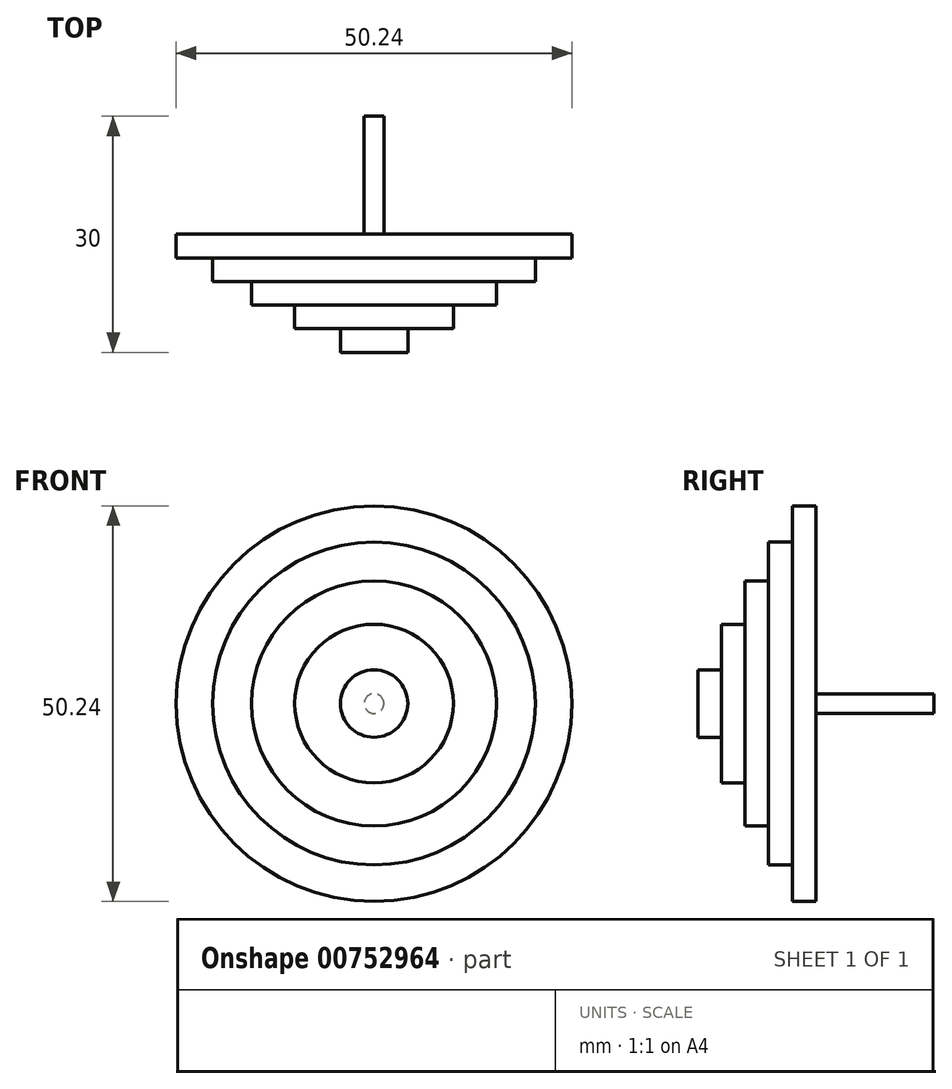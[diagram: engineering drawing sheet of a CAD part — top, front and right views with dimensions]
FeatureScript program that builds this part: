
annotation { "Feature Type Name" : "Feature", "Feature Type Description" : "" }
export const myFeature = defineFeature(function(context is Context, id is Id, definition is map)
    precondition{}
    {
        {
            var Q0;
            Q0=qCreatedBy(makeId("Front.planeOp"),FACE);
            var sketch = newSketch(context, id + "F0", { "sketchPlane" : qUnion([Q0])});
            skCircle(sketch, "E0", {"center": v(0, 0) * mm, "radius": 25.12 * mm});
            skCircle(sketch, "E1", {"center": v(0, 0) * mm, "radius": 20.5 * mm});
            skCircle(sketch, "E2", {"center": v(0, 0) * mm, "radius": 15.56 * mm});
            skCircle(sketch, "E3", {"center": v(0, 0) * mm, "radius": 10.08 * mm});
            skCircle(sketch, "E4", {"center": v(0, 0) * mm, "radius": 4.28 * mm});
            skCircle(sketch, "E5", {"center": v(0, 0) * mm, "radius": 1.25 * mm});
            skSolve(sketch);
        }
        {
            var Q0;
            Q0=makeQuery(id+"F0.imprint","IMPRINT",FACE,{"disambiguationData":[TD([[makeQuery(id+"F0.imprint","IMPRINT",EDGE,{"derivedFrom":sQuery(id+"F0.wireOp",EDGE,"E0")}),1.0]])]});
            extrude(context, id + "F1", {"entities" : qUnion([Q0]), "depth" : 3 * mm, "offsetDistance" : 25 * mm});
        }
        {
            var Q0;
            Q0=makeQuery(id+"F0.imprint","IMPRINT",FACE,{"disambiguationData":[TD([[makeQuery(id+"F0.imprint","IMPRINT",EDGE,{"derivedFrom":sQuery(id+"F0.wireOp",EDGE,"E1")}),1.0]])]});
            extrude(context, id + "F2", {"entities" : qUnion([Q0]), "operationType" : NewBodyOperationType.ADD, "depth" : 6 * mm, "offsetDistance" : 25 * mm});
        }
        {
            var Q0;
            Q0=makeQuery(id+"F0.imprint","IMPRINT",FACE,{"disambiguationData":[TD([[makeQuery(id+"F0.imprint","IMPRINT",EDGE,{"derivedFrom":sQuery(id+"F0.wireOp",EDGE,"E2")}),1.0]])]});
            extrude(context, id + "F3", {"entities" : qUnion([Q0]), "operationType" : NewBodyOperationType.ADD, "depth" : 9 * mm, "offsetDistance" : 25 * mm});
        }
        {
            var Q0;
            Q0=makeQuery(id+"F0.imprint","IMPRINT",FACE,{"disambiguationData":[TD([[makeQuery(id+"F0.imprint","IMPRINT",EDGE,{"derivedFrom":sQuery(id+"F0.wireOp",EDGE,"E3")}),1.0]])]});
            extrude(context, id + "F4", {"entities" : qUnion([Q0]), "operationType" : NewBodyOperationType.ADD, "depth" : 12 * mm, "offsetDistance" : 25 * mm});
        }
        {
            var Q0;
            Q0=makeQuery(id+"F0.imprint","IMPRINT",FACE,{"disambiguationData":[TD([[makeQuery(id+"F0.imprint","IMPRINT",EDGE,{"derivedFrom":sQuery(id+"F0.wireOp",EDGE,"E4")}),1.0]])]});
            extrude(context, id + "F5", {"entities" : qUnion([Q0]), "operationType" : NewBodyOperationType.ADD, "depth" : 15 * mm, "offsetDistance" : 25 * mm});
        }
        {
            var Q0;
            Q0=makeQuery(id+"F0.imprint","IMPRINT",FACE,{"disambiguationData":[TD([[makeQuery(id+"F0.imprint","IMPRINT",EDGE,{"derivedFrom":sQuery(id+"F0.wireOp",EDGE,"E5")}),1.0]])]});
            extrude(context, id + "F6", {"entities" : qUnion([Q0]), "operationType" : NewBodyOperationType.ADD, "depth" : 15 * mm, "offsetDistance" : 25 * mm});
        }
        {
            var Q0;
            Q0=makeQuery(id+"F0.imprint","IMPRINT",FACE,{"disambiguationData":[TD([[makeQuery(id+"F0.imprint","IMPRINT",EDGE,{"derivedFrom":sQuery(id+"F0.wireOp",EDGE,"E5")}),1.0]])]});
            extrude(context, id + "F7", {"entities" : qUnion([Q0]), "operationType" : NewBodyOperationType.ADD, "oppositeDirection" : true, "depth" : 15 * mm, "offsetDistance" : 25 * mm});
        }
    });
